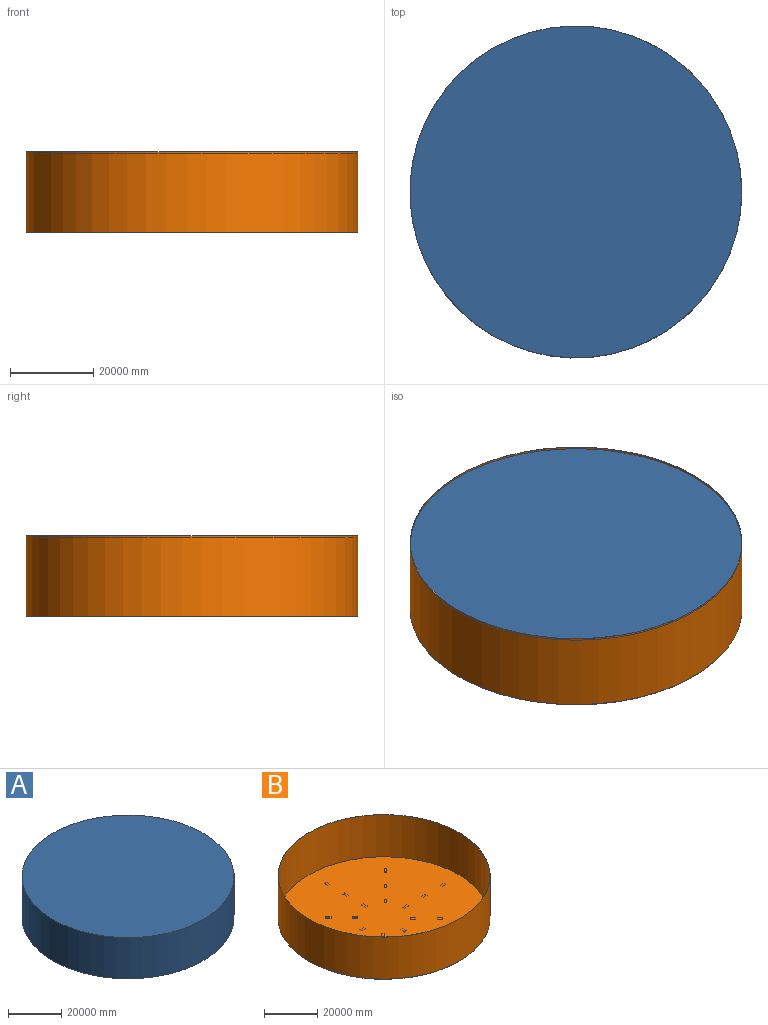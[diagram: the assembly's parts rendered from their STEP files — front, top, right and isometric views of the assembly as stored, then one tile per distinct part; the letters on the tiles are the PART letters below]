
ASSEMBLY  parts=2 mates=1
PART A: 3 faces, bbox 79921.2x79921.2x19000 mm
  f0: cylinder r=39960.6mm len=79921.2mm, axis (0,0,-1), area 4770517240.9mm2, adj f1,f2
  f1: plane 79921.2x79921.2mm, normal (0,0,1), area 5016650822.6mm2, adj f0
  f2: plane 79921.2x79921.2mm, normal (0,0,-1), area 5016650822.6mm2, adj f0
PART B: 125 faces, bbox 80000x80000x19500 mm
  f0: cylinder r=40000mm len=80000mm, axis (0,0,-1), area 4900884539.6mm2, adj f1,f2
  f1: plane 80000x80000mm, normal (0,0,1), area 9897423.2mm2, adj f0,f3
  f2: plane 80000x80000mm, normal (0,0,-1), area 5026548245.7mm2, adj f0
  f3: cylinder r=39960.6mm len=79921.2mm, axis (0,0,1), area 4886164622mm2, adj f1,f4
  f4: plane 79921.2x79921.2mm, normal (0,0,1), area 4968650822.6mm2, adj f3,f5,f6,f7,f8,f10,f11,f12
  f5: plane 1414.21x1414.21mm, normal (-0.71,0.71,0), area 100000mm2, adj f4,f6,f8,f9
  f6: plane 707.11x707.11mm, normal (-0.71,-0.71,0), area 50000mm2, adj f4,f5,f7,f9
  f7: plane 1414.21x1414.21mm, normal (0.71,-0.71,0), area 100000mm2, adj f4,f6,f8,f9
  f8: plane 707.11x707.11mm, normal (0.71,0.71,0), area 50000mm2, adj f4,f5,f7,f9
  f9: plane 2121.32x2121.32mm, normal (0,0,1), area 2000000mm2, adj f5,f6,f7,f8
  f10: plane 1000x50mm, normal (0,1,0), area 50000mm2, adj f4,f11,f13,f14
  f11: plane 2000x50mm, normal (-1,0,0), area 100000mm2, adj f4,f10,f12,f14
  f12: plane 1000x50mm, normal (0,-1,0), area 50000mm2, adj f4,f11,f13,f14
  f13: plane 2000x50mm, normal (1,0,0), area 100000mm2, adj f4,f10,f12,f14
  f14: plane 2000x1000mm, normal (0,0,1), area 2000000mm2, adj f10,f11,f12,f13
  f15: plane 707.11x707.11mm, normal (-0.71,0.71,0), area 50000mm2, adj f4,f16,f18,f19
  f16: plane 1414.21x1414.21mm, normal (-0.71,-0.71,0), area 100000mm2, adj f4,f15,f17,f19
  f17: plane 707.11x707.11mm, normal (0.71,-0.71,0), area 50000mm2, adj f4,f16,f18,f19
  f18: plane 1414.21x1414.21mm, normal (0.71,0.71,0), area 100000mm2, adj f4,f15,f17,f19
  f19: plane 2121.32x2121.32mm, normal (0,0,1), area 2000000mm2, adj f15,f16,f17,f18
  f20: plane 1000x50mm, normal (-1,0,0), area 50000mm2, adj f4,f21,f23,f24
  f21: plane 2000x50mm, normal (0,-1,0), area 100000mm2, adj f4,f20,f22,f24
  f22: plane 1000x50mm, normal (1,0,0), area 50000mm2, adj f4,f21,f23,f24
  f23: plane 2000x50mm, normal (0,1,0), area 100000mm2, adj f4,f20,f22,f24
  f24: plane 2000x1000mm, normal (0,0,1), area 2000000mm2, adj f20,f21,f22,f23
  f25: plane 707.11x707.11mm, normal (-0.71,-0.71,0), area 50000mm2, adj f4,f26,f28,f29
  f26: plane 1414.21x1414.21mm, normal (0.71,-0.71,0), area 100000mm2, adj f4,f25,f27,f29
  f27: plane 707.11x707.11mm, normal (0.71,0.71,0), area 50000mm2, adj f4,f26,f28,f29
  f28: plane 1414.21x1414.21mm, normal (-0.71,0.71,0), area 100000mm2, adj f4,f25,f27,f29
  f29: plane 2121.32x2121.32mm, normal (0,0,1), area 2000000mm2, adj f25,f26,f27,f28
  f30: plane 1000x50mm, normal (0,-1,0), area 50000mm2, adj f4,f31,f33,f34
  f31: plane 2000x50mm, normal (1,0,0), area 100000mm2, adj f4,f30,f32,f34
  f32: plane 1000x50mm, normal (0,1,0), area 50000mm2, adj f4,f31,f33,f34
  f33: plane 2000x50mm, normal (-1,0,0), area 100000mm2, adj f4,f30,f32,f34
  f34: plane 2000x1000mm, normal (0,0,1), area 2000000mm2, adj f30,f31,f32,f33
  f35: plane 707.11x707.11mm, normal (0.71,-0.71,0), area 50000mm2, adj f4,f36,f38,f39
  f36: plane 1414.21x1414.21mm, normal (0.71,0.71,0), area 100000mm2, adj f4,f35,f37,f39
  f37: plane 707.11x707.11mm, normal (-0.71,0.71,0), area 50000mm2, adj f4,f36,f38,f39
  f38: plane 1414.21x1414.21mm, normal (-0.71,-0.71,0), area 100000mm2, adj f4,f35,f37,f39
  f39: plane 2121.32x2121.32mm, normal (0,0,1), area 2000000mm2, adj f35,f36,f37,f38
  f40: plane 1000x50mm, normal (1,0,0), area 50000mm2, adj f4,f41,f43,f44
  f41: plane 2000x50mm, normal (0,1,0), area 100000mm2, adj f4,f40,f42,f44
  f42: plane 1000x50mm, normal (-1,0,0), area 50000mm2, adj f4,f41,f43,f44
  f43: plane 2000x50mm, normal (0,-1,0), area 100000mm2, adj f4,f40,f42,f44
  f44: plane 2000x1000mm, normal (0,0,1), area 2000000mm2, adj f40,f41,f42,f43
  f45: plane 1000x50mm, normal (0,-1,0), area 50000mm2, adj f4,f46,f48,f49
  f46: plane 2000x50mm, normal (1,0,0), area 100000mm2, adj f4,f45,f47,f49
  f47: plane 1000x50mm, normal (0,1,0), area 50000mm2, adj f4,f46,f48,f49
  f48: plane 2000x50mm, normal (-1,0,0), area 100000mm2, adj f4,f45,f47,f49
  f49: plane 2000x1000mm, normal (0,0,1), area 2000000mm2, adj f45,f46,f47,f48
  f50: plane 1000x50mm, normal (0,-1,0), area 50000mm2, adj f4,f51,f53,f54
  f51: plane 2000x50mm, normal (1,0,0), area 100000mm2, adj f4,f50,f52,f54
  f52: plane 1000x50mm, normal (0,1,0), area 50000mm2, adj f4,f51,f53,f54
  f53: plane 2000x50mm, normal (-1,0,0), area 100000mm2, adj f4,f50,f52,f54
  f54: plane 2000x1000mm, normal (0,0,1), area 2000000mm2, adj f50,f51,f52,f53
  f55: plane 1414.21x1414.21mm, normal (0.71,0.71,0), area 100000mm2, adj f4,f56,f58,f59
  f56: plane 707.11x707.11mm, normal (-0.71,0.71,0), area 50000mm2, adj f4,f55,f57,f59
  f57: plane 1414.21x1414.21mm, normal (-0.71,-0.71,0), area 100000mm2, adj f4,f56,f58,f59
  f58: plane 707.11x707.11mm, normal (0.71,-0.71,0), area 50000mm2, adj f4,f55,f57,f59
  f59: plane 2121.32x2121.32mm, normal (0,0,1), area 2000000mm2, adj f55,f56,f57,f58
  f60: plane 2000x50mm, normal (0,1,0), area 100000mm2, adj f4,f61,f63,f64
  f61: plane 1000x50mm, normal (-1,0,0), area 50000mm2, adj f4,f60,f62,f64
  f62: plane 2000x50mm, normal (0,-1,0), area 100000mm2, adj f4,f61,f63,f64
  f63: plane 1000x50mm, normal (1,0,0), area 50000mm2, adj f4,f60,f62,f64
  f64: plane 2000x1000mm, normal (0,0,1), area 2000000mm2, adj f60,f61,f62,f63
  f65: plane 1414.21x1414.21mm, normal (-0.71,0.71,0), area 100000mm2, adj f4,f66,f68,f69
  f66: plane 707.11x707.11mm, normal (-0.71,-0.71,0), area 50000mm2, adj f4,f65,f67,f69
  f67: plane 1414.21x1414.21mm, normal (0.71,-0.71,0), area 100000mm2, adj f4,f66,f68,f69
  f68: plane 707.11x707.11mm, normal (0.71,0.71,0), area 50000mm2, adj f4,f65,f67,f69
  f69: plane 2121.32x2121.32mm, normal (0,0,1), area 2000000mm2, adj f65,f66,f67,f68
  f70: plane 2000x50mm, normal (-1,0,0), area 100000mm2, adj f4,f71,f73,f74
  f71: plane 1000x50mm, normal (0,-1,0), area 50000mm2, adj f4,f70,f72,f74
  f72: plane 2000x50mm, normal (1,0,0), area 100000mm2, adj f4,f71,f73,f74
  f73: plane 1000x50mm, normal (0,1,0), area 50000mm2, adj f4,f70,f72,f74
  f74: plane 2000x1000mm, normal (0,0,1), area 2000000mm2, adj f70,f71,f72,f73
  f75: plane 1414.21x1414.21mm, normal (-0.71,-0.71,0), area 100000mm2, adj f4,f76,f78,f79
  f76: plane 707.11x707.11mm, normal (0.71,-0.71,0), area 50000mm2, adj f4,f75,f77,f79
  f77: plane 1414.21x1414.21mm, normal (0.71,0.71,0), area 100000mm2, adj f4,f76,f78,f79
  f78: plane 707.11x707.11mm, normal (-0.71,0.71,0), area 50000mm2, adj f4,f75,f77,f79
  f79: plane 2121.32x2121.32mm, normal (0,0,1), area 2000000mm2, adj f75,f76,f77,f78
  f80: plane 2000x50mm, normal (0,-1,0), area 100000mm2, adj f4,f81,f83,f84
  f81: plane 1000x50mm, normal (1,0,0), area 50000mm2, adj f4,f80,f82,f84
  f82: plane 2000x50mm, normal (0,1,0), area 100000mm2, adj f4,f81,f83,f84
  f83: plane 1000x50mm, normal (-1,0,0), area 50000mm2, adj f4,f80,f82,f84
  f84: plane 2000x1000mm, normal (0,0,1), area 2000000mm2, adj f80,f81,f82,f83
  f85: plane 1414.21x1414.21mm, normal (0.71,-0.71,0), area 100000mm2, adj f4,f86,f88,f89
  f86: plane 707.11x707.11mm, normal (0.71,0.71,0), area 50000mm2, adj f4,f85,f87,f89
  f87: plane 1414.21x1414.21mm, normal (-0.71,0.71,0), area 100000mm2, adj f4,f86,f88,f89
  f88: plane 707.11x707.11mm, normal (-0.71,-0.71,0), area 50000mm2, adj f4,f85,f87,f89
  f89: plane 2121.32x2121.32mm, normal (0,0,1), area 2000000mm2, adj f85,f86,f87,f88
  f90: plane 1414.21x1414.21mm, normal (0.71,0.71,0), area 100000mm2, adj f4,f91,f93,f94
  f91: plane 707.11x707.11mm, normal (-0.71,0.71,0), area 50000mm2, adj f4,f90,f92,f94
  f92: plane 1414.21x1414.21mm, normal (-0.71,-0.71,0), area 100000mm2, adj f4,f91,f93,f94
  f93: plane 707.11x707.11mm, normal (0.71,-0.71,0), area 50000mm2, adj f4,f90,f92,f94
  f94: plane 2121.32x2121.32mm, normal (0,0,1), area 2000000mm2, adj f90,f91,f92,f93
  f95: plane 2000x50mm, normal (0,1,0), area 100000mm2, adj f4,f96,f98,f99
  f96: plane 1000x50mm, normal (-1,0,0), area 50000mm2, adj f4,f95,f97,f99
  f97: plane 2000x50mm, normal (0,-1,0), area 100000mm2, adj f4,f96,f98,f99
  f98: plane 1000x50mm, normal (1,0,0), area 50000mm2, adj f4,f95,f97,f99
  f99: plane 2000x1000mm, normal (0,0,1), area 2000000mm2, adj f95,f96,f97,f98
  f100: plane 1414.21x1414.21mm, normal (-0.71,0.71,0), area 100000mm2, adj f4,f101,f103,f104
  f101: plane 707.11x707.11mm, normal (-0.71,-0.71,0), area 50000mm2, adj f4,f100,f102,f104
  f102: plane 1414.21x1414.21mm, normal (0.71,-0.71,0), area 100000mm2, adj f4,f101,f103,f104
  f103: plane 707.11x707.11mm, normal (0.71,0.71,0), area 50000mm2, adj f4,f100,f102,f104
  f104: plane 2121.32x2121.32mm, normal (0,0,1), area 2000000mm2, adj f100,f101,f102,f103
  f105: plane 2000x50mm, normal (-1,0,0), area 100000mm2, adj f4,f106,f108,f109
  f106: plane 1000x50mm, normal (0,-1,0), area 50000mm2, adj f4,f105,f107,f109
  f107: plane 2000x50mm, normal (1,0,0), area 100000mm2, adj f4,f106,f108,f109
  f108: plane 1000x50mm, normal (0,1,0), area 50000mm2, adj f4,f105,f107,f109
  f109: plane 2000x1000mm, normal (0,0,1), area 2000000mm2, adj f105,f106,f107,f108
  f110: plane 1414.21x1414.21mm, normal (-0.71,-0.71,0), area 100000mm2, adj f4,f111,f113,f114
  f111: plane 707.11x707.11mm, normal (0.71,-0.71,0), area 50000mm2, adj f4,f110,f112,f114
  f112: plane 1414.21x1414.21mm, normal (0.71,0.71,0), area 100000mm2, adj f4,f111,f113,f114
  f113: plane 707.11x707.11mm, normal (-0.71,0.71,0), area 50000mm2, adj f4,f110,f112,f114
  f114: plane 2121.32x2121.32mm, normal (0,0,1), area 2000000mm2, adj f110,f111,f112,f113
  f115: plane 2000x50mm, normal (0,-1,0), area 100000mm2, adj f4,f116,f118,f119
  f116: plane 1000x50mm, normal (1,0,0), area 50000mm2, adj f4,f115,f117,f119
  f117: plane 2000x50mm, normal (0,1,0), area 100000mm2, adj f4,f116,f118,f119
  f118: plane 1000x50mm, normal (-1,0,0), area 50000mm2, adj f4,f115,f117,f119
  f119: plane 2000x1000mm, normal (0,0,1), area 2000000mm2, adj f115,f116,f117,f118
  f120: plane 1414.21x1414.21mm, normal (0.71,-0.71,0), area 100000mm2, adj f4,f121,f123,f124
  f121: plane 707.11x707.11mm, normal (0.71,0.71,0), area 50000mm2, adj f4,f120,f122,f124
  f122: plane 1414.21x1414.21mm, normal (-0.71,0.71,0), area 100000mm2, adj f4,f121,f123,f124
  f123: plane 707.11x707.11mm, normal (-0.71,-0.71,0), area 50000mm2, adj f4,f120,f122,f124
  f124: plane 2121.32x2121.32mm, normal (0,0,1), area 2000000mm2, adj f120,f121,f122,f123
PLACE A t=(-1044.88,2527.59,-5019.03)mm
PLACE B t=(-1044.88,2527.59,-5058.43)mm
MATE cylindrical A.f0 <-> B.f3  axis (0,0,-1) through (-1044.88,2527.59,-5019.03)mm
